# Revit family: SENT400S
name_source: partatom
category: Mechanical Equipment
revit_build: Autodesk Revit MEP 2013 (Build: 20120221_2030(x64)
units: mm (PartAtom-declared; Revit-internal decimal feet)

## types (1)
- SENT400S
    AC Frequency Input = 50Hz nominal
    AC Voltage Input = 220-240 V AC (single phase))
    Category = Sentinel D-Box Single Fan
    Country of Manufacture = UK
    Height = 458mm
    IP Rating  External (WP) = IPX5
    IP Rating  Internal = IPX2
    Length (excluding Spigots) = 710mm
    Length (including Spigots) = 808mm
    Manufacturer - Name = Vent-Axia Ltd
    Manufacturer - Website = www.vent-axia.com
    Motor Rating = 450 Watts (max)
    Operating Temperature = (-10C to +40C)
    Operational and Maintenance Manual = http://www.vent-axia.com
    Options = Weatherproofed and Constant Pressure options
    Part Number = SENT400S
    Product Description = Sentinel D-Box Single Fan
    Spigot Diameter = 400mm
    Warranty period = Unit 2 years,Motor 5 years
    Weight = 36Kg
    Width (excluding controller) = 568mm
    Width (including controller) = 661mm

## geometry (parser evidence)
native form markers: Sweep x1
no freeform markers — native parametric forms only
